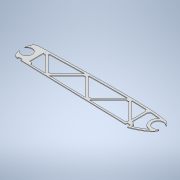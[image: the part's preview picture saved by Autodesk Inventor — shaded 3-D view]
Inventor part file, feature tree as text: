
AUTODESK INVENTOR PART (.ipt)
format: ipt  version: 2022 (Build 260153000, 153)  size: 382,464 bytes
history: native  units: mm
features: extrude x1, sketch x1
ambient origin geometry x8: Origin, YZ Plane, XZ Plane, XY Plane, X Axis, Y Axis, Z Axis, Center Point
bodies: Body1 (feature_tree)
feature tree (2):
  extrude  "Extrusion5"  Depth=368.759386mm
  sketch  "Sketch1"  dims[d31=34.456mm d50=368.759386mm d57=16.0mm d69=8.0mm d70=23.0mm d71=8.0mm d73=16.0mm d80=19.0mm d81=16.0mm d82=1.0mm d83=1.0mm d84=1.0mm d85=1.0mm d86=1.0mm d87=0.8mm d88=1.0mm d90=19.0mm d94=5.0mm d95=5.0mm d105=5.0mm d106=5.0mm d108=2.0mm d109=19.0mm d114=5.0mm d115=5.0mm d116=24.0mm d117=2.5mm d118=2.5mm d123=2.5mm d124=2.5mm d125=10.0mm d126=24.0mm d127=24.0mm d128=27.0mm d135=0.5mm d136=45.0deg d139=7.0mm d165=45.0deg d169=27.0mm d175=90.0deg d181=45.0deg d185=7.0mm d186=45.0deg d190=7.0mm d191=45.0deg d197=90.0deg d203=90.0deg d206=7.0mm d207=1.0mm d208=0.0mm]
